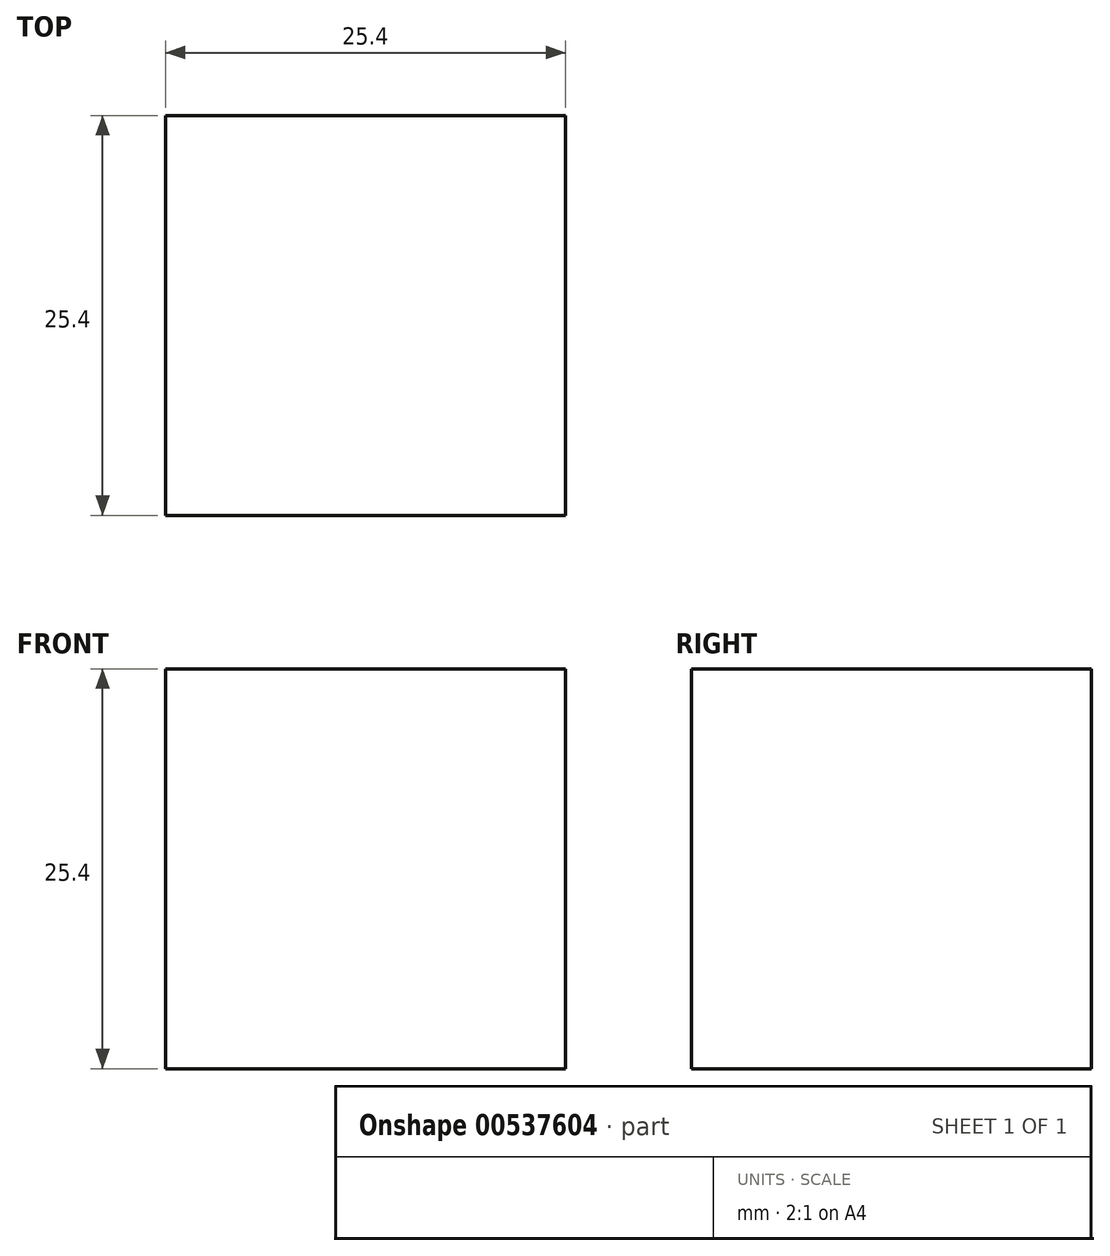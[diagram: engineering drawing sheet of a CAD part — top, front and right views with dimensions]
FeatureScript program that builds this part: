
annotation { "Feature Type Name" : "Feature", "Feature Type Description" : "" }
export const myFeature = defineFeature(function(context is Context, id is Id, definition is map)
    precondition{}
    {
        {
            var Q0;
            Q0=qCreatedBy(makeId("Top.planeOp"),FACE);
            var sketch = newSketch(context, id + "F0", { "sketchPlane" : qUnion([Q0])});
            skLineSegment(sketch, "E0.bottom", {"start": v(-12.7, -12.7) * mm, "end": v(12.7, -12.7) * mm});
            skLineSegment(sketch, "E0.top", {"start": v(-12.7, 12.7) * mm, "end": v(12.7, 12.7) * mm});
            skLineSegment(sketch, "E0.left", {"start": v(-12.7, -12.7) * mm, "end": v(-12.7, 12.7) * mm});
            skLineSegment(sketch, "E0.right", {"start": v(12.7, -12.7) * mm, "end": v(12.7, 12.7) * mm});
            skPoint(sketch, "E0.middle", {"position": v(0, 0) * mm});
            skSolve(sketch);
        }
        {
            var Q0;
            Q0=makeQuery(id+"F0.imprint","IMPRINT",FACE,{"disambiguationData":[TD([[makeQuery(id+"F0.imprint","IMPRINT",EDGE,{"derivedFrom":sQuery(id+"F0.wireOp",EDGE,"E0.bottom")}),1.0]])]});
            extrude(context, id + "F1", {"entities" : qUnion([Q0]), "depth" : 25.4 * mm, "offsetDistance" : 25.4 * mm});
        }
    });
